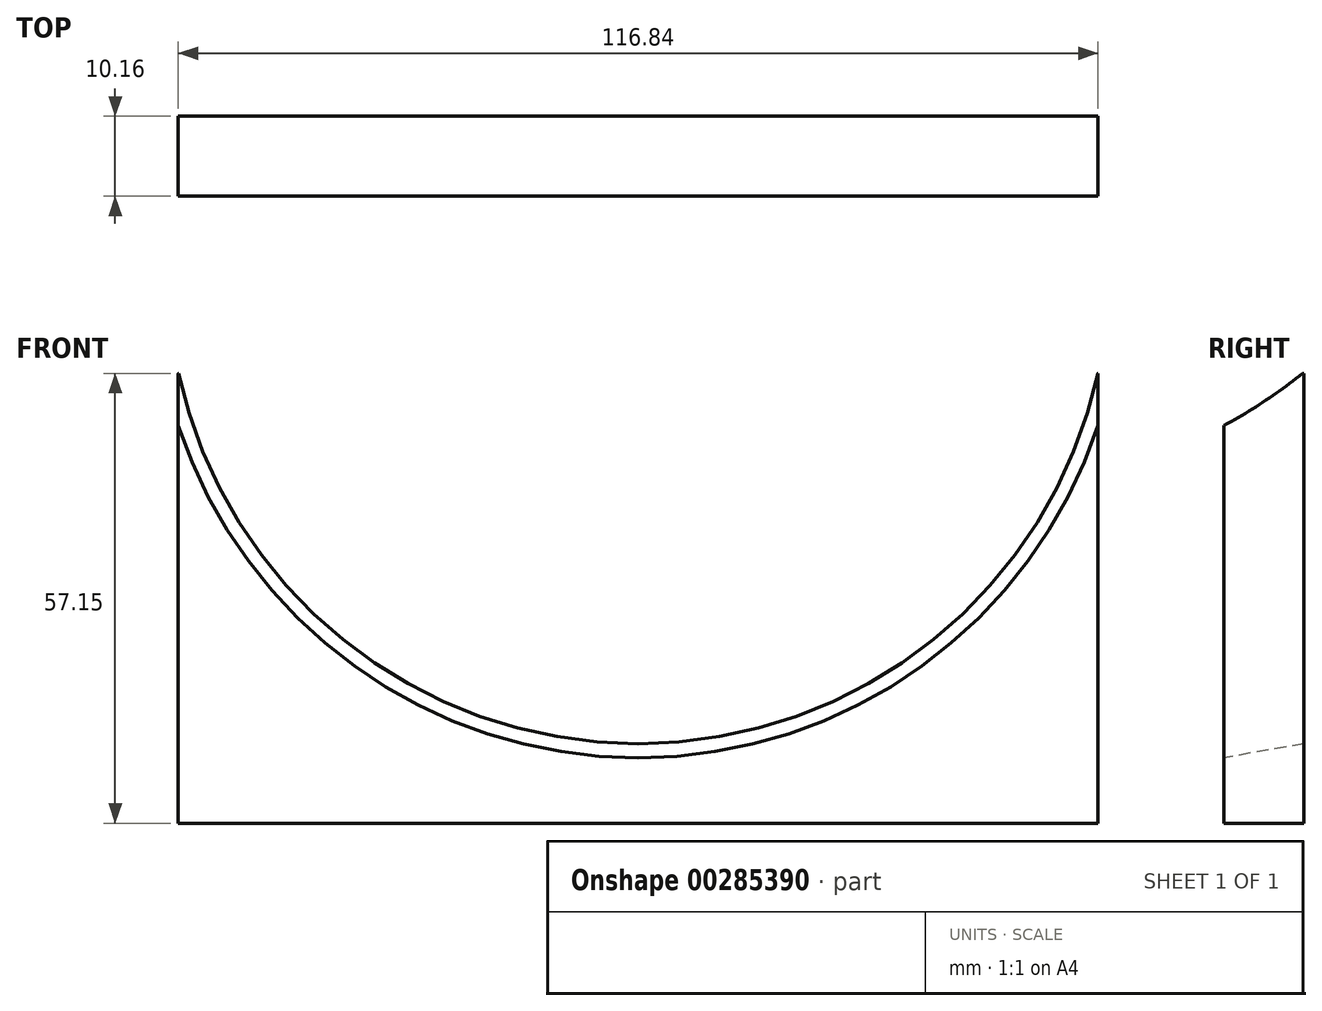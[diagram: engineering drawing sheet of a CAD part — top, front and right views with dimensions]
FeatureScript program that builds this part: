
annotation { "Feature Type Name" : "Feature", "Feature Type Description" : "" }
export const myFeature = defineFeature(function(context is Context, id is Id, definition is map)
    precondition{}
    {
        {
            var Q0;
            Q0=qCreatedBy(makeId("Front.planeOp"),FACE);
            var sketch = newSketch(context, id + "F0", { "sketchPlane" : qUnion([Q0])});
            skLineSegment(sketch, "E0.bottom", {"start": v(0, 0) * mm, "end": v(-116.84, 0) * mm});
            skLineSegment(sketch, "E0.top", {"start": v(0, 57.15) * mm, "end": v(-2.7, 57.15) * mm});
            skLineSegment(sketch, "E0.left", {"start": v(0, 0) * mm, "end": v(0, 57.15) * mm});
            skLineSegment(sketch, "E0.right", {"start": v(-116.84, 0) * mm, "end": v(-116.84, 57.15) * mm});
            skPoint(sketch, "E1.endSnap0", {"position": v(-58.42, 57.15) * mm});
            skPoint(sketch, "E2.endSnap0", {"position": v(-58.42, 6.35) * mm});
            skArc(sketch, "E3", {"start": v(-114.14, 57.15) * mm, "mid": v(-58.42, 12.7) * mm, "end": v(-2.7, 57.15) * mm});
            skLineSegment(sketch, "E4.trimOffspring", {"start": v(-114.14, 57.15) * mm, "end": v(-116.84, 57.15) * mm});
            skSolve(sketch);
        }
        {
            var Q0;
            Q0=makeQuery(id+"F0.imprint","IMPRINT",FACE,{"disambiguationData":[TD([[makeQuery(id+"F0.imprint","IMPRINT",EDGE,{"derivedFrom":sQuery(id+"F0.wireOp",EDGE,"E0.bottom")}),-1.0]])]});
            extrude(context, id + "F1", {"entities" : qUnion([Q0]), "depth" : 10.16 * mm});
        }
        {
            var Q0;
            Q0=makeQuery(id+"F1.opExtrude","CAP_EDGE",EDGE,{"disambiguationData":[OSD([sQuery(id+"F0.wireOp",EDGE,"E3")])],"isStart":false});
            chamfer(context, id + "F2", {"entities" : qUnion([Q0]), "chamferType" : ChamferType.OFFSET_ANGLE, "width" : 24.9 * mm, "oppositeDirection" : false, "angle" : 10 * degree, "tangentPropagation" : true});
        }
    });
